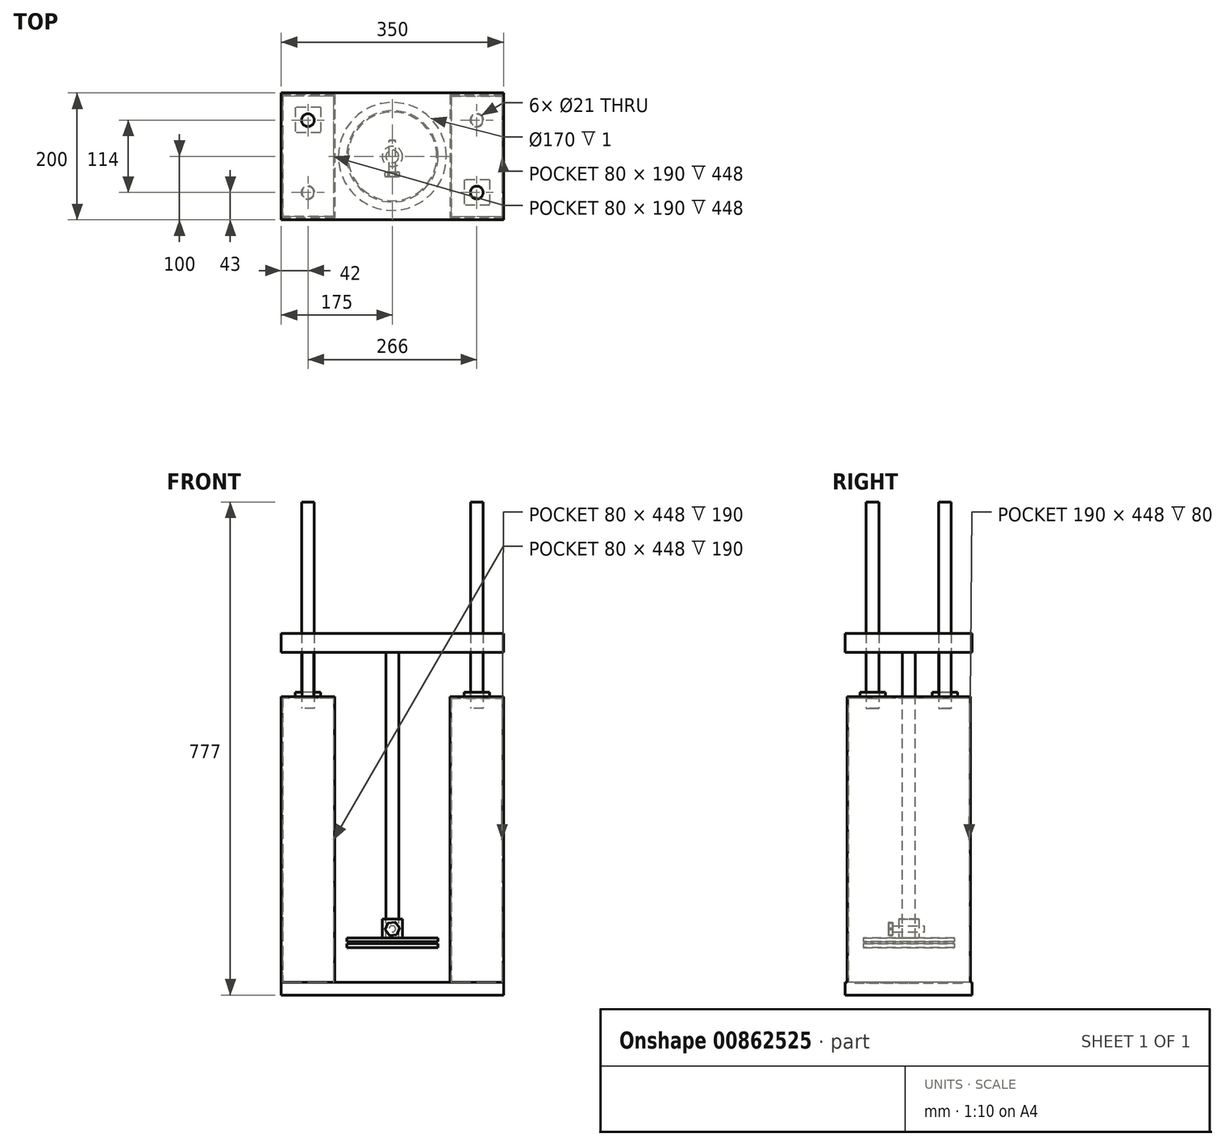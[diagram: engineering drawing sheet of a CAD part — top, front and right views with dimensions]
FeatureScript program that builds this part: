
annotation { "Feature Type Name" : "Feature", "Feature Type Description" : "" }
export const myFeature = defineFeature(function(context is Context, id is Id, definition is map)
    precondition{}
    {
        {
            var Q0;
            Q0=qCreatedBy(makeId("Top.planeOp"),FACE);
            var sketch = newSketch(context, id + "F0", { "sketchPlane" : qUnion([Q0])});
            skLineSegment(sketch, "E0.bottom", {"start": v(175, 100) * mm, "end": v(-175, 100) * mm});
            skLineSegment(sketch, "E0.top", {"start": v(175, -100) * mm, "end": v(-175, -100) * mm});
            skLineSegment(sketch, "E0.left", {"start": v(175, 100) * mm, "end": v(175, -100) * mm});
            skLineSegment(sketch, "E0.right", {"start": v(-175, 100) * mm, "end": v(-175, -100) * mm});
            skPoint(sketch, "E0.middle", {"position": v(0, 0) * mm});
            skSolve(sketch);
        }
        {
            var Q0;
            Q0=makeQuery(id+"F0.imprint","IMPRINT",FACE,{"disambiguationData":[TD([[makeQuery(id+"F0.imprint","IMPRINT",EDGE,{"derivedFrom":sQuery(id+"F0.wireOp",EDGE,"E0.bottom")}),1.0]])]});
            extrude(context, id + "F1", {"entities" : qUnion([Q0]), "depth" : 20 * mm, "offsetDistance" : 25 * mm});
        }
        {
            var Q0;
            Q0=makeQuery(id+"F1.opExtrude","CAP_FACE",FACE,{"disambiguationData":[OSD([sQuery(id+"F0.wireOp",EDGE,"E0.bottom"),sQuery(id+"F0.wireOp",EDGE,"E0.top"),sQuery(id+"F0.wireOp",EDGE,"E0.left"),sQuery(id+"F0.wireOp",EDGE,"E0.right")])],"isStart":false});
            var sketch = newSketch(context, id + "F2", { "sketchPlane" : qUnion([Q0])});
            skLineSegment(sketch, "E1.bottom", {"start": v(-93, 95) * mm, "end": v(-173, 95) * mm});
            skLineSegment(sketch, "E1.top", {"start": v(-93, -95) * mm, "end": v(-173, -95) * mm});
            skLineSegment(sketch, "E1.left", {"start": v(-93, 95) * mm, "end": v(-93, -95) * mm});
            skLineSegment(sketch, "E1.right", {"start": v(-173, 95) * mm, "end": v(-173, -95) * mm});
            skPoint(sketch, "E1.middle", {"position": v(-133, 0) * mm});
            skLineSegment(sketch, "E2.bottom", {"start": v(-91, 97) * mm, "end": v(-175, 97) * mm});
            skLineSegment(sketch, "E2.top", {"start": v(-91, -97) * mm, "end": v(-175, -97) * mm});
            skLineSegment(sketch, "E2.left", {"start": v(-91, 97) * mm, "end": v(-91, -97) * mm});
            skLineSegment(sketch, "E2.right", {"start": v(-175, 97) * mm, "end": v(-175, -97) * mm});
            skPoint(sketch, "E3.MirrorP", {"position": v(133, 0) * mm});
            skLineSegment(sketch, "E4.MirrorCS", {"start": v(91, -97) * mm, "end": v(175, -97) * mm});
            skLineSegment(sketch, "E5.MirrorCS", {"start": v(93, 95) * mm, "end": v(93, -95) * mm});
            skLineSegment(sketch, "E6.MirrorCS", {"start": v(173, 95) * mm, "end": v(173, -95) * mm});
            skLineSegment(sketch, "E7.MirrorCS", {"start": v(91, 97) * mm, "end": v(175, 97) * mm});
            skLineSegment(sketch, "E8.MirrorCS", {"start": v(93, 95) * mm, "end": v(173, 95) * mm});
            skLineSegment(sketch, "E9.MirrorCS", {"start": v(175, 97) * mm, "end": v(175, -97) * mm});
            skLineSegment(sketch, "E10.MirrorCS", {"start": v(93, -95) * mm, "end": v(173, -95) * mm});
            skLineSegment(sketch, "E11.MirrorCS", {"start": v(91, 97) * mm, "end": v(91, -97) * mm});
            skSolve(sketch);
        }
        {
            var Q0;
            Q0=makeQuery(id+"F2.imprint","IMPRINT",FACE,{"disambiguationData":[TD([[makeQuery(id+"F2.imprint","IMPRINT",EDGE,{"derivedFrom":sQuery(id+"F2.wireOp",EDGE,"E1.bottom")}),-1.0]])]});
            var Q1;
            Q1=makeQuery(id+"F2.imprint","IMPRINT",FACE,{"disambiguationData":[TD([[makeQuery(id+"F2.imprint","IMPRINT",EDGE,{"derivedFrom":sQuery(id+"F2.wireOp",EDGE,"E4.MirrorCS")}),1.0]])]});
            extrude(context, id + "F3", {"entities" : qUnion([Q0, Q1]), "operationType" : NewBodyOperationType.ADD, "depth" : 450 * mm, "offsetDistance" : 25 * mm});
        }
        {
            var Q0;
            Q0=makeQuery(id+"F3.opExtrude","CAP_FACE",FACE,{"disambiguationData":[OSD([sQuery(id+"F2.wireOp",EDGE,"E1.bottom"),sQuery(id+"F2.wireOp",EDGE,"E1.top"),sQuery(id+"F2.wireOp",EDGE,"E1.left"),sQuery(id+"F2.wireOp",EDGE,"E1.right"),sQuery(id+"F2.wireOp",EDGE,"E2.bottom"),sQuery(id+"F2.wireOp",EDGE,"E2.top"),sQuery(id+"F2.wireOp",EDGE,"E2.left"),sQuery(id+"F2.wireOp",EDGE,"E2.right")])],"isStart":false});
            var sketch = newSketch(context, id + "F4", { "sketchPlane" : qUnion([Q0])});
            skLineSegment(sketch, "E12.bottom", {"start": v(-91, 97) * mm, "end": v(-175, 97) * mm});
            skLineSegment(sketch, "E12.top", {"start": v(-91, -97) * mm, "end": v(-175, -97) * mm});
            skLineSegment(sketch, "E12.left", {"start": v(-91, 97) * mm, "end": v(-91, -97) * mm});
            skLineSegment(sketch, "E12.right", {"start": v(-175, 97) * mm, "end": v(-175, -97) * mm});
            skLineSegment(sketch, "E13.MirrorCS", {"start": v(91, 97) * mm, "end": v(175, 97) * mm});
            skLineSegment(sketch, "E14.MirrorCS", {"start": v(91, -97) * mm, "end": v(175, -97) * mm});
            skLineSegment(sketch, "E15.MirrorCS", {"start": v(175, 97) * mm, "end": v(175, -97) * mm});
            skLineSegment(sketch, "E16.MirrorCS", {"start": v(91, 97) * mm, "end": v(91, -97) * mm});
            skCircle(sketch, "E17", {"center": v(-133, -57) * mm, "radius": 10.5 * mm});
            skCircle(sketch, "E18", {"center": v(133, 57) * mm, "radius": 10.5 * mm});
            skCircle(sketch, "E19.MirrorC", {"center": v(-133, 57) * mm, "radius": 10.5 * mm});
            skCircle(sketch, "E20.MirrorC", {"center": v(133, -57) * mm, "radius": 10.5 * mm});
            skSolve(sketch);
        }
        {
            var Q0;
            Q0=makeQuery(id+"F4.imprint","IMPRINT",FACE,{"disambiguationData":[TD([[makeQuery(id+"F4.imprint","IMPRINT",EDGE,{"derivedFrom":sQuery(id+"F4.wireOp",EDGE,"E17")}),-1.0]])]});
            var Q1;
            Q1=makeQuery(id+"F4.imprint","IMPRINT",FACE,{"disambiguationData":[TD([[makeQuery(id+"F4.imprint","IMPRINT",EDGE,{"derivedFrom":sQuery(id+"F4.wireOp",EDGE,"E13.MirrorCS")}),-1.0]])]});
            extrude(context, id + "F5", {"entities" : qUnion([Q0, Q1]), "operationType" : NewBodyOperationType.ADD, "oppositeDirection" : true, "depth" : 2 * mm, "offsetDistance" : 25 * mm});
        }
        {
            var Q0;
            {var subQ0=sQuery(id+"F2.wireOp",EDGE,"E1.right");var subQ1=sQuery(id+"F2.wireOp",EDGE,"E1.left");var subQ2=sQuery(id+"F2.wireOp",EDGE,"E1.top");var subQ3=sQuery(id+"F2.wireOp",EDGE,"E1.bottom");Q0=makeQuery(id+"F5.boolean.opBoolean","MERGE",FACE,{"derivedFrom":[makeQuery(id+"F3.opExtrude","CAP_FACE",FACE,{"disambiguationData":[OSD([subQ3,subQ2,subQ1,subQ0,sQuery(id+"F2.wireOp",EDGE,"E2.bottom"),sQuery(id+"F2.wireOp",EDGE,"E2.top"),sQuery(id+"F2.wireOp",EDGE,"E2.left"),sQuery(id+"F2.wireOp",EDGE,"E2.right")])],"isStart":false}),makeQuery(id+"F5.opExtrude","CAP_FACE",FACE,{"disambiguationData":[OSD([subQ3,subQ2,subQ1,subQ0,sQuery(id+"F4.wireOp",EDGE,"E17")])],"isStart":true})]});}
            var sketch = newSketch(context, id + "F6", { "sketchPlane" : qUnion([Q0])});
            skCircle(sketch, "E21", {"center": v(-133, -57) * mm, "radius": 9.5 * mm});
            skCircle(sketch, "E22", {"center": v(133, 57) * mm, "radius": 9.5 * mm});
            skSolve(sketch);
        }
        {
            var Q0;
            Q0=makeQuery(id+"F6.imprint","IMPRINT",FACE,{"disambiguationData":[TD([[makeQuery(id+"F6.imprint","IMPRINT",EDGE,{"derivedFrom":sQuery(id+"F6.wireOp",EDGE,"E21")}),1.0]])]});
            var Q1;
            Q1=makeQuery(id+"F6.imprint","IMPRINT",FACE,{"disambiguationData":[TD([[makeQuery(id+"F6.imprint","IMPRINT",EDGE,{"derivedFrom":sQuery(id+"F6.wireOp",EDGE,"E22")}),1.0]])]});
            extrude(context, id + "F7", {"entities" : qUnion([Q0, Q1]), "depth" : 70 * mm, "offsetDistance" : 25 * mm});
        }
        {
            var Q0;
            Q0=makeQuery(id+"F7.opExtrude","CAP_FACE",FACE,{"disambiguationData":[OSD([sQuery(id+"F6.wireOp",EDGE,"E22")])],"isStart":false});
            var sketch = newSketch(context, id + "F8", { "sketchPlane" : qUnion([Q0])});
            skLineSegment(sketch, "E23.bottom", {"start": v(175, 100) * mm, "end": v(-175, 100) * mm});
            skLineSegment(sketch, "E23.top", {"start": v(175, -100) * mm, "end": v(-175, -100) * mm});
            skLineSegment(sketch, "E23.left", {"start": v(175, 100) * mm, "end": v(175, -100) * mm});
            skLineSegment(sketch, "E23.right", {"start": v(-175, 100) * mm, "end": v(-175, -100) * mm});
            skSolve(sketch);
        }
        {
            var Q0;
            Q0=makeQuery(id+"F8.imprint","IMPRINT",FACE,{"disambiguationData":[TD([[makeQuery(id+"F8.imprint","IMPRINT",EDGE,{"derivedFrom":sQuery(id+"F8.wireOp",EDGE,"E23.bottom")}),1.0]])]});
            var Q1;
            Q1=makeQuery(id+"F8.imprint","IMPRINT",FACE,{"disambiguationData":[TD([[makeQuery(id+"F8.imprint","IMPRINT",EDGE,{"derivedFrom":makeQuery(id+"F7.opExtrude","CAP_EDGE",EDGE,{"disambiguationData":[OSD([sQuery(id+"F6.wireOp",EDGE,"E22")])],"isStart":false})}),1.0]])]});
            extrude(context, id + "F9", {"entities" : qUnion([Q0, Q1]), "depth" : 30 * mm, "offsetDistance" : 25 * mm});
        }
        {
            var Q0;
            {var subQ0=sQuery(id+"F0.wireOp",EDGE,"E0.bottom");var subQ1=sQuery(id+"F0.wireOp",EDGE,"E0.right");var subQ2=sQuery(id+"F0.wireOp",EDGE,"E0.top");var subQ3=sQuery(id+"F0.wireOp",EDGE,"E0.left");Q0=makeQuery(id+"F3.boolean.opBoolean","SPLIT",FACE,{"disambiguationData":[TD([makeQuery(id+"F1.opExtrude","SWEPT_FACE",FACE,{"disambiguationData":[OSD([subQ0])]})])],"derivedFrom":makeQuery(id+"F1.opExtrude","CAP_FACE",FACE,{"disambiguationData":[OSD([subQ0,subQ2,subQ3,subQ1])],"isStart":false})});}
            var sketch = newSketch(context, id + "F10", { "sketchPlane" : qUnion([Q0])});
            skCircle(sketch, "E24", {"center": v(0, 0) * mm, "radius": 85 * mm});
            skSolve(sketch);
        }
        {
            var Q0;
            Q0=makeQuery(id+"F10.imprint","IMPRINT",FACE,{"disambiguationData":[TD([[makeQuery(id+"F10.imprint","IMPRINT",EDGE,{"derivedFrom":sQuery(id+"F10.wireOp",EDGE,"E24")}),1.0]])]});
            extrude(context, id + "F11", {"entities" : qUnion([Q0]), "operationType" : NewBodyOperationType.REMOVE, "oppositeDirection" : true, "depth" : 1 * mm, "offsetDistance" : 25 * mm});
        }
        {
            var Q0;
            Q0=makeQuery(id+"F9.opExtrude","CAP_FACE",FACE,{"disambiguationData":[OSD([sQuery(id+"F8.wireOp",EDGE,"E23.bottom"),sQuery(id+"F8.wireOp",EDGE,"E23.top"),sQuery(id+"F8.wireOp",EDGE,"E23.left"),sQuery(id+"F8.wireOp",EDGE,"E23.right")])],"isStart":true});
            var sketch = newSketch(context, id + "F12", { "sketchPlane" : qUnion([Q0])});
            skCircle(sketch, "E25", {"center": v(0, 0) * mm, "radius": 10 * mm});
            skSolve(sketch);
        }
        {
            var Q0;
            Q0=makeQuery(id+"F12.imprint","IMPRINT",FACE,{"disambiguationData":[TD([[makeQuery(id+"F12.imprint","IMPRINT",EDGE,{"derivedFrom":sQuery(id+"F12.wireOp",EDGE,"E25")}),1.0]])]});
            extrude(context, id + "F13", {"entities" : qUnion([Q0]), "depth" : 450 * mm, "offsetDistance" : 25 * mm});
        }
        {
            var Q0;
            Q0=qCreatedBy(makeId("Front.planeOp"),FACE);
            var sketch = newSketch(context, id + "F14", { "sketchPlane" : qUnion([Q0])});
            skLineSegment(sketch, "E26", {"start": v(0, 90) * mm, "end": v(72, 90) * mm});
            skLineSegment(sketch, "E27", {"start": v(72, 75) * mm, "end": v(0, 75) * mm});
            skLineSegment(sketch, "E28", {"start": v(0, 75) * mm, "end": v(0, 90) * mm});
            skLineSegment(sketch, "E29", {"start": v(72, 90) * mm, "end": v(72, 84) * mm});
            skLineSegment(sketch, "E30", {"start": v(72, 81) * mm, "end": v(70, 81) * mm});
            skLineSegment(sketch, "E31", {"start": v(70, 84) * mm, "end": v(70, 81) * mm});
            skLineSegment(sketch, "E32", {"start": v(70, 84) * mm, "end": v(72, 84) * mm});
            skLineSegment(sketch, "E33", {"start": v(72, 81) * mm, "end": v(72, 75) * mm});
            skLineSegment(sketch, "E34", {"start": v(16, 90) * mm, "end": v(16, 120) * mm});
            skLineSegment(sketch, "E35", {"start": v(16, 120) * mm, "end": v(0, 120) * mm});
            skLineSegment(sketch, "E36", {"start": v(0, 120) * mm, "end": v(0, 90) * mm});
            skSolve(sketch);
        }
        {
            var Q0;
            Q0=makeQuery(id+"F14.imprint","IMPRINT",FACE,{"disambiguationData":[TD([[makeQuery(id+"F14.imprint","IMPRINT",EDGE,{"derivedFrom":sQuery(id+"F14.wireOp",EDGE,"E26")}),-1.0]])]});
            var Q1;
            {var subQ2=sQuery(id+"F14.wireOp",EDGE,"E34");Q1=makeQuery(id+"F14.imprint","IMPRINT",FACE,{"disambiguationData":[TD([[makeQuery(id+"F14.imprint","IMPRINT",EDGE,{"derivedFrom":subQ2}),1.0]])]});}
            var Q2;
            Q2=sQuery(id+"F14.wireOp",EDGE,"E28");
            revolve(context, id + "F15", {"surfaceOperationType" : NewSurfaceOperationType.NEW, "entities" : qUnion([Q0, Q1]), "axis" : qUnion([Q2]), "revolveType" : RevolveType.FULL});
        }
        {
            var Q0;
            Q0=qCreatedBy(makeId("Front.planeOp"),FACE);
            var sketch = newSketch(context, id + "F16", { "sketchPlane" : qUnion([Q0])});
            skCircle(sketch, "E37", {"center": v(0, 104.3) * mm, "radius": 5 * mm});
            skSolve(sketch);
        }
        {
            var Q0;
            Q0 = qSketchRegion(id + "F16", true);
            extrude(context, id + "F17", {"entities" : qUnion([Q0]), "depth" : 25 * mm, "offsetDistance" : 25 * mm, "hasSecondDirection" : true, "secondDirectionOppositeDirection" : true, "secondDirectionDepth" : 25 * mm});
        }
        {
            var Q0;
            Q0=makeQuery(id+"F17.opExtrude","CAP_FACE",FACE,{"disambiguationData":[OSD([sQuery(id+"F16.wireOp",EDGE,"E37")])],"isStart":false});
            var sketch = newSketch(context, id + "F18", { "sketchPlane" : qUnion([Q0])});
            skCircle(sketch, "E38", {"center": v(0, 104.3) * mm, "radius": 10 * mm});
            skCircle(sketch, "E39.cCircle", {"center": v(0, 104.3) * mm, "radius": 10 * mm, "construction": true});
            skLineSegment(sketch, "E39.0", {"start": v(4.57, 114.9) * mm, "end": v(11.47, 105.64) * mm});
            skLineSegment(sketch, "E39.1", {"start": v(11.47, 105.64) * mm, "end": v(6.9, 95.03) * mm});
            skLineSegment(sketch, "E39.2", {"start": v(6.9, 95.03) * mm, "end": v(-4.57, 93.69) * mm});
            skLineSegment(sketch, "E39.3", {"start": v(-4.57, 93.69) * mm, "end": v(-11.47, 102.95) * mm});
            skLineSegment(sketch, "E39.4", {"start": v(-11.47, 102.95) * mm, "end": v(-6.9, 113.55) * mm});
            skLineSegment(sketch, "E39.5", {"start": v(-6.9, 113.55) * mm, "end": v(4.57, 114.9) * mm});
            skPoint(sketch, "E39.0.midPoint", {"position": v(8.02, 110.27) * mm});
            skSolve(sketch);
        }
        {
            var Q0;
            Q0=makeQuery(id+"F18.imprint","IMPRINT",FACE,{"disambiguationData":[TD([[makeQuery(id+"F18.imprint","IMPRINT",EDGE,{"derivedFrom":sQuery(id+"F18.wireOp",EDGE,"E38")}),1.0]])]});
            var Q1;
            Q1=makeQuery(id+"F18.imprint","IMPRINT",FACE,{"disambiguationData":[TD([[makeQuery(id+"F18.imprint","IMPRINT",EDGE,{"derivedFrom":makeQuery(id+"F17.opExtrude","CAP_EDGE",EDGE,{"disambiguationData":[OSD([sQuery(id+"F16.wireOp",EDGE,"E37")])],"isStart":false})}),1.0]])]});
            var Q2;
            {var subQ0=sQuery(id+"F18.wireOp",EDGE,"E39.5");var subQ1=sQuery(id+"F18.wireOp",EDGE,"E38");var subQ2=makeQuery(id+"F18.imprint","INTERSECT",VERTEX,{"derivedFrom":[subQ1,subQ0]});Q2=makeQuery(id+"F18.imprint","IMPRINT",FACE,{"disambiguationData":[TD([[makeQuery(id+"F18.imprint","IMPRINT",EDGE,{"disambiguationData":[TD([[subQ2,-1.0]])],"derivedFrom":subQ1}),-1.0]])]});}
            var Q3;
            {var subQ0=sQuery(id+"F18.wireOp",EDGE,"E39.4");var subQ1=sQuery(id+"F18.wireOp",EDGE,"E38");var subQ2=makeQuery(id+"F18.imprint","INTERSECT",VERTEX,{"derivedFrom":[subQ1,subQ0]});Q3=makeQuery(id+"F18.imprint","IMPRINT",FACE,{"disambiguationData":[TD([[makeQuery(id+"F18.imprint","IMPRINT",EDGE,{"disambiguationData":[TD([[subQ2,-1.0]])],"derivedFrom":subQ1}),-1.0]])]});}
            var Q4;
            {var subQ0=sQuery(id+"F18.wireOp",EDGE,"E39.3");var subQ1=sQuery(id+"F18.wireOp",EDGE,"E38");var subQ2=makeQuery(id+"F18.imprint","INTERSECT",VERTEX,{"derivedFrom":[subQ1,subQ0]});Q4=makeQuery(id+"F18.imprint","IMPRINT",FACE,{"disambiguationData":[TD([[makeQuery(id+"F18.imprint","IMPRINT",EDGE,{"disambiguationData":[TD([[subQ2,-1.0]])],"derivedFrom":subQ1}),-1.0]])]});}
            var Q5;
            {var subQ0=sQuery(id+"F18.wireOp",EDGE,"E39.2");var subQ1=sQuery(id+"F18.wireOp",EDGE,"E38");var subQ2=makeQuery(id+"F18.imprint","INTERSECT",VERTEX,{"derivedFrom":[subQ1,subQ0]});Q5=makeQuery(id+"F18.imprint","IMPRINT",FACE,{"disambiguationData":[TD([[makeQuery(id+"F18.imprint","IMPRINT",EDGE,{"disambiguationData":[TD([[subQ2,-1.0]])],"derivedFrom":subQ1}),-1.0]])]});}
            var Q6;
            {var subQ0=sQuery(id+"F18.wireOp",EDGE,"E39.0");var subQ1=sQuery(id+"F18.wireOp",EDGE,"E38");var subQ2=makeQuery(id+"F18.imprint","INTERSECT",VERTEX,{"derivedFrom":[subQ1,subQ0]});Q6=makeQuery(id+"F18.imprint","IMPRINT",FACE,{"disambiguationData":[TD([[makeQuery(id+"F18.imprint","IMPRINT",EDGE,{"disambiguationData":[TD([[subQ2,1.0]])],"derivedFrom":subQ1}),-1.0]])]});}
            var Q7;
            {var subQ0=sQuery(id+"F18.wireOp",EDGE,"E39.5");var subQ1=sQuery(id+"F18.wireOp",EDGE,"E38");var subQ2=makeQuery(id+"F18.imprint","INTERSECT",VERTEX,{"derivedFrom":[subQ1,subQ0]});Q7=makeQuery(id+"F18.imprint","IMPRINT",FACE,{"disambiguationData":[TD([[makeQuery(id+"F18.imprint","IMPRINT",EDGE,{"disambiguationData":[TD([[subQ2,1.0]])],"derivedFrom":subQ1}),-1.0]])]});}
            extrude(context, id + "F19", {"entities" : qUnion([Q0, Q1, Q2, Q3, Q4, Q5, Q6, Q7]), "operationType" : NewBodyOperationType.ADD, "depth" : 7 * mm, "offsetDistance" : 25 * mm});
        }
        {
            var Q0;
            Q0=makeQuery(id+"F19.opExtrude","CAP_FACE",FACE,{"disambiguationData":[OSD([sQuery(id+"F18.wireOp",EDGE,"E39.0"),sQuery(id+"F18.wireOp",EDGE,"E39.1"),sQuery(id+"F18.wireOp",EDGE,"E39.2"),sQuery(id+"F18.wireOp",EDGE,"E39.3"),sQuery(id+"F18.wireOp",EDGE,"E39.4"),sQuery(id+"F18.wireOp",EDGE,"E39.5")])],"isStart":false});
            var Q1;
            Q1=makeQuery(id+"F19.opExtrude","CAP_FACE",FACE,{"disambiguationData":[OSD([sQuery(id+"F18.wireOp",EDGE,"E39.0"),sQuery(id+"F18.wireOp",EDGE,"E39.1"),sQuery(id+"F18.wireOp",EDGE,"E39.2"),sQuery(id+"F18.wireOp",EDGE,"E39.3"),sQuery(id+"F18.wireOp",EDGE,"E39.4"),sQuery(id+"F18.wireOp",EDGE,"E39.5")])],"isStart":true});
            fillet(context, id + "F20", {"entities" : qUnion([Q0, Q1]), "radius" : 1 * mm, "tangentPropagation" : true, "allowEdgeOverflow" : false});
        }
        {
            var Q0;
            {var subQ0=sQuery(id+"F2.wireOp",EDGE,"E1.right");var subQ1=sQuery(id+"F2.wireOp",EDGE,"E1.left");var subQ2=sQuery(id+"F2.wireOp",EDGE,"E1.top");var subQ3=sQuery(id+"F2.wireOp",EDGE,"E1.bottom");Q0=makeQuery(id+"F5.boolean.opBoolean","MERGE",FACE,{"derivedFrom":[makeQuery(id+"F3.opExtrude","CAP_FACE",FACE,{"disambiguationData":[OSD([subQ3,subQ2,subQ1,subQ0,sQuery(id+"F2.wireOp",EDGE,"E2.bottom"),sQuery(id+"F2.wireOp",EDGE,"E2.top"),sQuery(id+"F2.wireOp",EDGE,"E2.left"),sQuery(id+"F2.wireOp",EDGE,"E2.right")])],"isStart":false}),makeQuery(id+"F5.opExtrude","CAP_FACE",FACE,{"disambiguationData":[OSD([subQ3,subQ2,subQ1,subQ0,sQuery(id+"F4.wireOp",EDGE,"E17"),sQuery(id+"F4.wireOp",EDGE,"E19.MirrorC")])],"isStart":true})]});}
            var sketch = newSketch(context, id + "F21", { "sketchPlane" : qUnion([Q0])});
            skLineSegment(sketch, "E40.bottom", {"start": v(-113, 77) * mm, "end": v(-153, 77) * mm});
            skLineSegment(sketch, "E40.top", {"start": v(-113, 37) * mm, "end": v(-153, 37) * mm});
            skLineSegment(sketch, "E40.left", {"start": v(-113, 77) * mm, "end": v(-113, 37) * mm});
            skLineSegment(sketch, "E40.right", {"start": v(-153, 77) * mm, "end": v(-153, 37) * mm});
            skPoint(sketch, "E40.middle", {"position": v(-133, 57) * mm});
            skLineSegment(sketch, "E41.bottom", {"start": v(153, -37) * mm, "end": v(113, -37) * mm});
            skLineSegment(sketch, "E41.top", {"start": v(153, -77) * mm, "end": v(113, -77) * mm});
            skLineSegment(sketch, "E41.left", {"start": v(153, -37) * mm, "end": v(153, -77) * mm});
            skLineSegment(sketch, "E41.right", {"start": v(113, -37) * mm, "end": v(113, -77) * mm});
            skPoint(sketch, "E41.middle", {"position": v(133, -57) * mm});
            skCircle(sketch, "E42", {"center": v(133, -57) * mm, "radius": 10.5 * mm});
            skCircle(sketch, "E43", {"center": v(-133, 57) * mm, "radius": 10.5 * mm});
            skSolve(sketch);
        }
        {
            var Q0;
            Q0=makeQuery(id+"F21.imprint","IMPRINT",FACE,{"disambiguationData":[TD([[makeQuery(id+"F21.imprint","IMPRINT",EDGE,{"derivedFrom":sQuery(id+"F21.wireOp",EDGE,"E40.bottom")}),1.0]])]});
            var Q1;
            Q1=makeQuery(id+"F21.imprint","IMPRINT",FACE,{"disambiguationData":[TD([[makeQuery(id+"F21.imprint","IMPRINT",EDGE,{"derivedFrom":sQuery(id+"F21.wireOp",EDGE,"E41.bottom")}),1.0]])]});
            extrude(context, id + "F22", {"entities" : qUnion([Q0, Q1]), "depth" : 7 * mm, "offsetDistance" : 25 * mm});
        }
        {
            var Q0;
            Q0=makeQuery(id+"F22.opExtrude","CAP_FACE",FACE,{"disambiguationData":[OSD([sQuery(id+"F21.wireOp",EDGE,"E40.bottom"),sQuery(id+"F21.wireOp",EDGE,"E40.top"),sQuery(id+"F21.wireOp",EDGE,"E40.left"),sQuery(id+"F21.wireOp",EDGE,"E40.right"),sQuery(id+"F21.wireOp",EDGE,"E43")])],"isStart":false});
            var sketch = newSketch(context, id + "F23", { "sketchPlane" : qUnion([Q0])});
            skCircle(sketch, "E44", {"center": v(-133, 57) * mm, "radius": 10 * mm});
            skCircle(sketch, "E45", {"center": v(133, -57) * mm, "radius": 10 * mm});
            skSolve(sketch);
        }
        {
            var Q0;
            Q0=makeQuery(id+"F23.imprint","IMPRINT",FACE,{"disambiguationData":[TD([[makeQuery(id+"F23.imprint","IMPRINT",EDGE,{"derivedFrom":sQuery(id+"F23.wireOp",EDGE,"E44")}),1.0]])]});
            var Q1;
            Q1=makeQuery(id+"F23.imprint","IMPRINT",FACE,{"disambiguationData":[TD([[makeQuery(id+"F23.imprint","IMPRINT",EDGE,{"derivedFrom":sQuery(id+"F23.wireOp",EDGE,"E45")}),1.0]])]});
            extrude(context, id + "F24", {"entities" : qUnion([Q0, Q1]), "depth" : 300 * mm, "offsetDistance" : 25 * mm, "hasSecondDirection" : true, "secondDirectionOppositeDirection" : true, "secondDirectionDepth" : 25 * mm});
        }
    });
